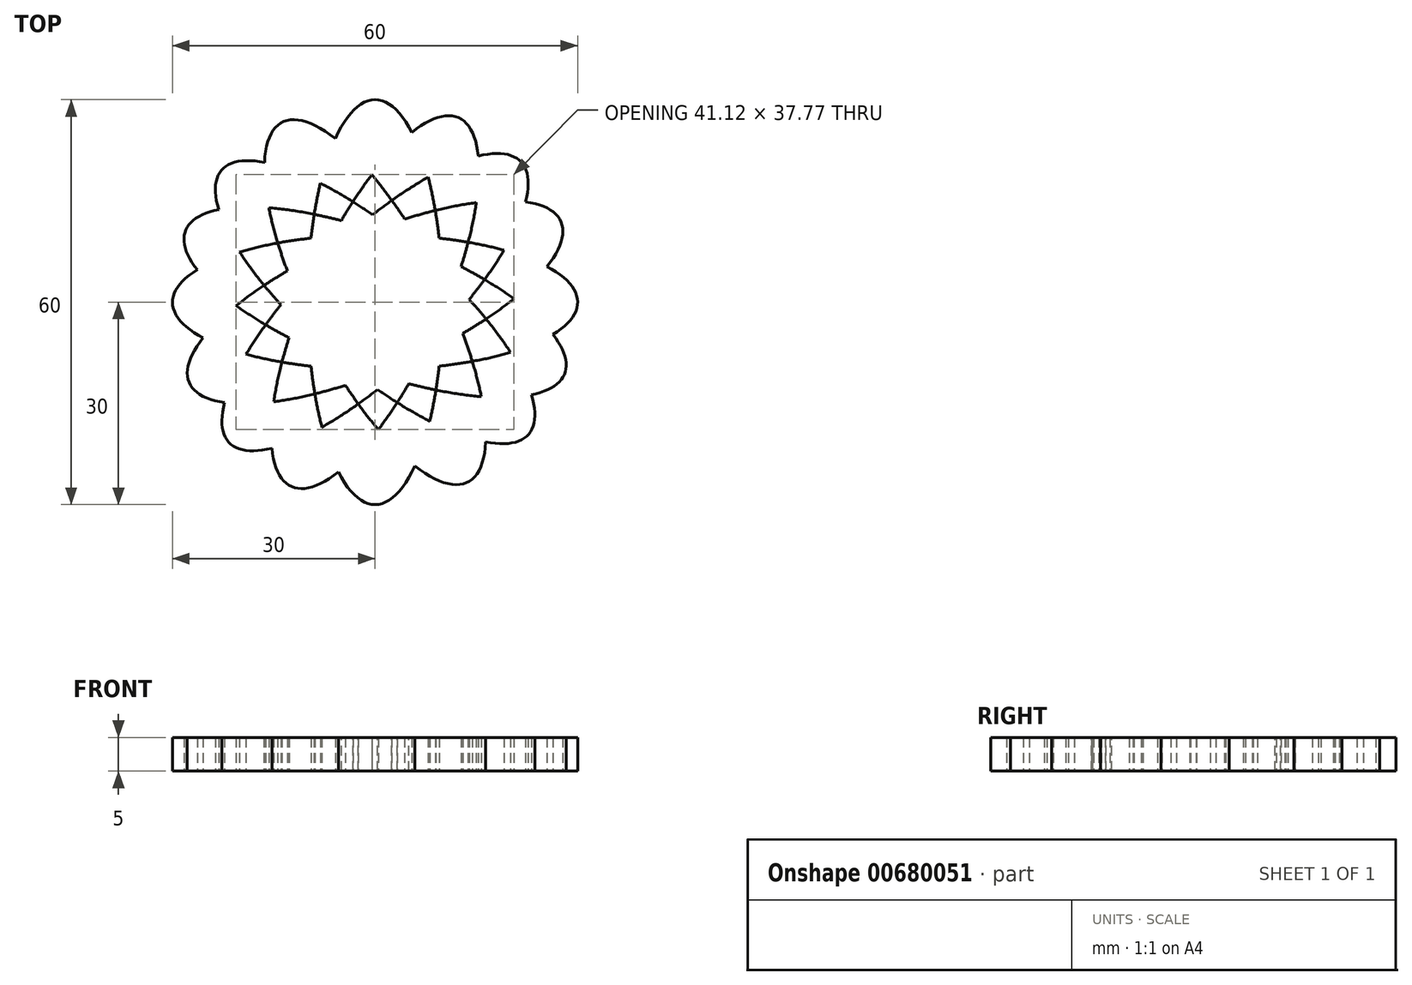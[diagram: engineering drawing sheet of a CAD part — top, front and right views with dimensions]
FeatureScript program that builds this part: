
annotation { "Feature Type Name" : "Feature", "Feature Type Description" : "" }
export const myFeature = defineFeature(function(context is Context, id is Id, definition is map)
    precondition{}
    {
        {
            var Q0;
            Q0=qCreatedBy(makeId("Top.planeOp"),FACE);
            var sketch = newSketch(context, id + "F0", { "sketchPlane" : qUnion([Q0])});
            skEllipticalArc(sketch, "E0", {});
            skEllipticalArc(sketch, "E1", {});
            skEllipticalArc(sketch, "E2", {});
            skEllipticalArc(sketch, "E3", {});
            skEllipticalArc(sketch, "E4", {});
            skEllipticalArc(sketch, "E5", {});
            skEllipticalArc(sketch, "E6", {});
            skEllipticalArc(sketch, "E7", {});
            skEllipticalArc(sketch, "E8.trimOffspring", {});
            skEllipticalArc(sketch, "E9.trimOffspring", {});
            skEllipticalArc(sketch, "E10.trimOffspring", {});
            skEllipticalArc(sketch, "E11.trimOffspring", {});
            skEllipticalArc(sketch, "E12.trimOffspring", {});
            skEllipticalArc(sketch, "E13.trimOffspring", {});
            skEllipticalArc(sketch, "E14.trimOffspring", {});
            skEllipticalArc(sketch, "E15.trimOffspring", {});
            skEllipticalArc(sketch, "E16.trimOffspring", {});
            skEllipticalArc(sketch, "E17.trimOffspring", {});
            skEllipticalArc(sketch, "E18.trimOffspring", {});
            skEllipticalArc(sketch, "E19.trimOffspring", {});
            skEllipticalArc(sketch, "E20.trimOffspring", {});
            skEllipticalArc(sketch, "E21.trimOffspring", {});
            skEllipticalArc(sketch, "E22.trimOffspring", {});
            skEllipticalArc(sketch, "E23.trimOffspring", {});
            skEllipticalArc(sketch, "E24.trimOffspring", {});
            skEllipticalArc(sketch, "E25.trimOffspring", {});
            skEllipticalArc(sketch, "E26.trimOffspring", {});
            skEllipticalArc(sketch, "E27.trimOffspring", {});
            skEllipticalArc(sketch, "E28.trimOffspring", {});
            skEllipticalArc(sketch, "E29.trimOffspring", {});
            skEllipticalArc(sketch, "E30.trimOffspring", {});
            skEllipticalArc(sketch, "E31.trimOffspring", {});
            skEllipticalArc(sketch, "E32", {});
            skEllipticalArc(sketch, "E33", {});
            skEllipticalArc(sketch, "E34", {});
            skEllipticalArc(sketch, "E35", {});
            skEllipticalArc(sketch, "E36", {});
            skEllipticalArc(sketch, "E37", {});
            skEllipticalArc(sketch, "E38", {});
            skEllipticalArc(sketch, "E39", {});
            skEllipticalArc(sketch, "E40", {});
            skEllipticalArc(sketch, "E41", {});
            skEllipticalArc(sketch, "E42", {});
            skEllipticalArc(sketch, "E43", {});
            skEllipticalArc(sketch, "E44", {});
            skEllipticalArc(sketch, "E45", {});
            skEllipticalArc(sketch, "E46", {});
            skEllipticalArc(sketch, "E47", {});
            const initialGuessF0  = {"E0": [0, 0, 0, -1, 0.03, 0.01, 5.707652658227705, 0], "E1": [0, 0, -1, 0, 0.03, 0.01, 2.642024951638131, 3.141592653589793], "E2": [0, 0, 0.719676517800556, 0.6943095201179845, 0.03, 0.01, 4.047013061400929, 5.402548984350965], "E3": [0, 0, -0.7581335094198967, 0.6520993650469777, 0.03, 0.01, 2.6137857632382424, 3.141592653589793], "E4": [0, 0, -0.45874326626276485, 0.8885688581413205, 0.03, 0.01, 2.511853225270534, 3.141592653589793], "E5": [0, 0, 0.41320832804158036, 0.9106365233379791, 0.03, 0.01, 4.109892639118385, 5.42593323517256], "E6": [0, 0, -0.9359348451973232, 0.35217320390038603, 0.03, 0.01, 2.653348630316495, 3.141592653589793], "E7": [0, 0, -0.9172268162763845, -0.3983653693576886, 0.03, 0.01, 2.584183450086654, 3.141592653589793], "E8.trimOffspring": [0, 0, 0, -1, 0.03, 0.01, 0.9425783349267141, 2.2361722457786577], "E9.trimOffspring": [0, 0, -0.45874326626276485, 0.8885688581413205, 0.03, 0.01, 3.998280747334294, 5.314885321650993], "E10.trimOffspring": [0, 0, -0.7581335094198967, 0.6520993650469777, 0.03, 0.01, 3.9802901965482214, 5.340606972252871], "E11.trimOffspring": [0, 0, -0.9359348451973232, 0.35217320390038603, 0.03, 0.01, 4.023758446463335, 5.426497213435084], "E12.trimOffspring": [0, 0, -1, 0, 0.03, 0.01, 4.022228976418415, 5.444487764221157], "E13.trimOffspring": [0, 0, 0.719676517800556, 0.6943095201179845, 0.03, 0.01, 5.78620703741481, 0], "E14.trimOffspring": [0, 0, -0.9172268162763845, -0.3983653693576886, 0.03, 0.01, 3.9988447255968187, 5.401019514306045], "E15.trimOffspring": [0, 0, 0.41320832804158036, 0.9106365233379791, 0.03, 0.01, 5.7629630431196155, 0], "E16.trimOffspring": [0, 0, 0.719676517800556, 0.6943095201179845, 0.03, 0.01, 0.9054204078111355, 2.260956330761171], "E17.trimOffspring": [0, 0, 0, -1, 0.03, 0.01, 2.566060004637914, 3.141592653589793], "E18.trimOffspring": [0, 0, 0.41320832804158036, 0.9106365233379791, 0.03, 0.01, 0.9682999855285929, 2.284340581582767], "E19.trimOffspring": [0, 0, -0.45874326626276485, 0.8885688581413205, 0.03, 0.01, 5.653445878860328, 0], "E20.trimOffspring": [0, 0, 0, -1, 0.03, 0.01, 4.084170988516508, 5.377764899368451], "E21.trimOffspring": [0, 0, -0.7581335094198967, 0.6520993650469777, 0.03, 0.01, 5.7553784168280355, 0], "E22.trimOffspring": [0, 0, -0.45874326626276485, 0.8885688581413205, 0.03, 0.01, 0.856688093744502, 2.1732926680612006], "E23.trimOffspring": [0, 0, -0.9359348451973232, 0.35217320390038603, 0.03, 0.01, 5.7949412839062875, 0], "E24.trimOffspring": [0, 0, -0.7581335094198967, 0.6520993650469777, 0.03, 0.01, 0.8386975429584291, 2.199014318663079], "E25.trimOffspring": [0, 0, -1, 0, 0.03, 0.01, 5.783617605227924, 0], "E26.trimOffspring": [0, 0, -0.9359348451973232, 0.35217320390038603, 0.03, 0.01, 0.8821657928735414, 2.284904559845293], "E27.trimOffspring": [0, 0, -0.9172268162763845, -0.3983653693576886, 0.03, 0.01, 5.725776103676448, 0], "E28.trimOffspring": [0, 0, -1, 0, 0.03, 0.01, 0.8806363228286226, 2.3028951106313644], "E29.trimOffspring": [0, 0, 0.719676517800556, 0.6943095201179845, 0.03, 0.01, 2.644614383825017, 3.141592653589793], "E30.trimOffspring": [0, 0, -0.9172268162763845, -0.3983653693576886, 0.03, 0.01, 0.857252072007026, 2.2594268607162515], "E31.trimOffspring": [0, 0, 0.41320832804158036, 0.9106365233379791, 0.03, 0.01, 2.6213703895298224, 3.141592653589793], "E32": [0, 0, -1, 0, 0.03, 0.01, 0, 0.5574092035031396], "E33": [0, 0, -0.9172268162763845, -0.3983653693576886, 0.03, 0.01, 0, 0.4969782697647762], "E34": [0, 0, 0.719676517800556, 0.6943095201179845, 0.03, 0.01, 3.141592653589793, 3.6618149176497643], "E35": [0, 0, 0.41320832804158036, 0.9106365233379791, 0.03, 0.01, 3.141592653589793, 3.7171253025416737], "E36": [0, 0, 0, -1, 0.03, 0.01, 0, 0.6297394283192591], "E37": [0, 0, -0.45874326626276485, 0.8885688581413205, 0.03, 0.01, 3.141592653589793, 3.6693995439413434], "E38": [0, 0, -0.7581335094198967, 0.6520993650469777, 0.03, 0.01, 3.141592653589793, 3.6298366768630923], "E39": [0, 0, -0.9359348451973232, 0.35217320390038603, 0.03, 0.01, 3.141592653589793, 3.6411603555414533], "E40": [0, 0, -1, 0, 0.03, 0.01, 3.141592653589793, 3.6990018570929326], "E41": [0, 0, -0.9172268162763845, -0.3983653693576886, 0.03, 0.01, 3.141592653589793, 3.6385709233545684], "E42": [0, 0, 0.719676517800556, 0.6943095201179845, 0.03, 0.01, 0, 0.5202222640599707], "E43": [0, 0, 0.41320832804158036, 0.9106365233379791, 0.03, 0.01, 0, 0.5755326489518812], "E44": [0, 0, 0, -1, 0.03, 0.01, 3.141592653589793, 3.7713320819090503], "E45": [0, 0, -0.45874326626276485, 0.8885688581413205, 0.03, 0.01, 0, 0.5278068903515505], "E46": [0, 0, -0.7581335094198967, 0.6520993650469777, 0.03, 0.01, 0, 0.48824402327329985], "E47": [0, 0, -0.9359348451973232, 0.35217320390038603, 0.03, 0.01, 0, 0.4995677019516617]};
            skSetInitialGuess(sketch, initialGuessF0);
            skSolve(sketch);
        }
        {
            var Q0;
            Q0=makeQuery(id+"F0.imprint","IMPRINT",FACE,{"disambiguationData":[TD([[makeQuery(id+"F0.imprint","IMPRINT",EDGE,{"derivedFrom":sQuery(id+"F0.wireOp",EDGE,"E0")}),1.0]])]});
            var Q1;
            {var subQ17=sQuery(id+"F0.wireOp",EDGE,"E2");var subQ21=sQuery(id+"F0.wireOp",EDGE,"E30.trimOffspring");var subQ22=makeQuery(id+"F0.imprint","INTERSECT",VERTEX,{"derivedFrom":[subQ17,subQ21]});Q1=makeQuery(id+"F0.imprint","IMPRINT",FACE,{"disambiguationData":[TD([[makeQuery(id+"F0.imprint","IMPRINT",EDGE,{"disambiguationData":[TD([[subQ22,-1.0]])],"derivedFrom":subQ17}),1.0]])]});}
            var Q2;
            {var subQ0=sQuery(id+"F0.wireOp",EDGE,"E14.trimOffspring");var subQ1=sQuery(id+"F0.wireOp",EDGE,"E9.trimOffspring");var subQ2=makeQuery(id+"F0.imprint","INTERSECT",VERTEX,{"derivedFrom":[subQ1,subQ0]});Q2=makeQuery(id+"F0.imprint","IMPRINT",FACE,{"disambiguationData":[TD([[makeQuery(id+"F0.imprint","IMPRINT",EDGE,{"disambiguationData":[TD([[subQ2,-1.0]])],"derivedFrom":subQ1}),1.0]])]});}
            var Q3;
            {var subQ0=sQuery(id+"F0.wireOp",EDGE,"E12.trimOffspring");var subQ1=sQuery(id+"F0.wireOp",EDGE,"E8.trimOffspring");var subQ2=makeQuery(id+"F0.imprint","INTERSECT",VERTEX,{"derivedFrom":[subQ1,subQ0]});Q3=makeQuery(id+"F0.imprint","IMPRINT",FACE,{"disambiguationData":[TD([[makeQuery(id+"F0.imprint","IMPRINT",EDGE,{"disambiguationData":[TD([[subQ2,-1.0]])],"derivedFrom":subQ1}),1.0]])]});}
            var Q4;
            {var subQ0=sQuery(id+"F0.wireOp",EDGE,"E11.trimOffspring");var subQ1=sQuery(id+"F0.wireOp",EDGE,"E8.trimOffspring");var subQ2=makeQuery(id+"F0.imprint","INTERSECT",VERTEX,{"derivedFrom":[subQ1,subQ0]});Q4=makeQuery(id+"F0.imprint","IMPRINT",FACE,{"disambiguationData":[TD([[makeQuery(id+"F0.imprint","IMPRINT",EDGE,{"disambiguationData":[TD([[subQ2,-1.0]])],"derivedFrom":subQ1}),1.0]])]});}
            var Q5;
            {var subQ0=sQuery(id+"F0.wireOp",EDGE,"E11.trimOffspring");var subQ1=sQuery(id+"F0.wireOp",EDGE,"E5");var subQ2=makeQuery(id+"F0.imprint","INTERSECT",VERTEX,{"derivedFrom":[subQ1,subQ0]});Q5=makeQuery(id+"F0.imprint","IMPRINT",FACE,{"disambiguationData":[TD([[makeQuery(id+"F0.imprint","IMPRINT",EDGE,{"disambiguationData":[TD([[subQ2,-1.0]])],"derivedFrom":subQ1}),1.0]])]});}
            var Q6;
            {var subQ0=sQuery(id+"F0.wireOp",EDGE,"E10.trimOffspring");var subQ1=sQuery(id+"F0.wireOp",EDGE,"E5");var subQ2=makeQuery(id+"F0.imprint","INTERSECT",VERTEX,{"derivedFrom":[subQ1,subQ0]});Q6=makeQuery(id+"F0.imprint","IMPRINT",FACE,{"disambiguationData":[TD([[makeQuery(id+"F0.imprint","IMPRINT",EDGE,{"disambiguationData":[TD([[subQ2,-1.0]])],"derivedFrom":subQ1}),1.0]])]});}
            var Q7;
            {var subQ0=sQuery(id+"F0.wireOp",EDGE,"E10.trimOffspring");var subQ1=sQuery(id+"F0.wireOp",EDGE,"E2");var subQ2=makeQuery(id+"F0.imprint","INTERSECT",VERTEX,{"derivedFrom":[subQ1,subQ0]});Q7=makeQuery(id+"F0.imprint","IMPRINT",FACE,{"disambiguationData":[TD([[makeQuery(id+"F0.imprint","IMPRINT",EDGE,{"disambiguationData":[TD([[subQ2,-1.0]])],"derivedFrom":subQ1}),1.0]])]});}
            var Q8;
            {var subQ0=sQuery(id+"F0.wireOp",EDGE,"E10.trimOffspring");var subQ1=sQuery(id+"F0.wireOp",EDGE,"E8.trimOffspring");var subQ2=makeQuery(id+"F0.imprint","INTERSECT",VERTEX,{"derivedFrom":[subQ1,subQ0]});Q8=makeQuery(id+"F0.imprint","IMPRINT",FACE,{"disambiguationData":[TD([[makeQuery(id+"F0.imprint","IMPRINT",EDGE,{"disambiguationData":[TD([[subQ2,-1.0]])],"derivedFrom":subQ1}),1.0]])]});}
            var Q9;
            {var subQ0=sQuery(id+"F0.wireOp",EDGE,"E9.trimOffspring");var subQ1=sQuery(id+"F0.wireOp",EDGE,"E2");var subQ2=makeQuery(id+"F0.imprint","INTERSECT",VERTEX,{"derivedFrom":[subQ1,subQ0]});Q9=makeQuery(id+"F0.imprint","IMPRINT",FACE,{"disambiguationData":[TD([[makeQuery(id+"F0.imprint","IMPRINT",EDGE,{"disambiguationData":[TD([[subQ2,-1.0]])],"derivedFrom":subQ1}),1.0]])]});}
            var Q10;
            {var subQ0=sQuery(id+"F0.wireOp",EDGE,"E9.trimOffspring");var subQ1=sQuery(id+"F0.wireOp",EDGE,"E2");var subQ2=makeQuery(id+"F0.imprint","INTERSECT",VERTEX,{"derivedFrom":[subQ1,subQ0]});Q10=makeQuery(id+"F0.imprint","IMPRINT",FACE,{"disambiguationData":[TD([[makeQuery(id+"F0.imprint","IMPRINT",EDGE,{"disambiguationData":[TD([[subQ2,-1.0]])],"derivedFrom":subQ1}),-1.0]])]});}
            var Q11;
            {var subQ0=sQuery(id+"F0.wireOp",EDGE,"E28.trimOffspring");var subQ1=sQuery(id+"F0.wireOp",EDGE,"E8.trimOffspring");var subQ2=makeQuery(id+"F0.imprint","INTERSECT",VERTEX,{"derivedFrom":[subQ1,subQ0]});Q11=makeQuery(id+"F0.imprint","IMPRINT",FACE,{"disambiguationData":[TD([[makeQuery(id+"F0.imprint","IMPRINT",EDGE,{"disambiguationData":[TD([[subQ2,-1.0]])],"derivedFrom":subQ1}),-1.0]])]});}
            var Q12;
            {var subQ0=sQuery(id+"F0.wireOp",EDGE,"E8.trimOffspring");var subQ1=sQuery(id+"F0.wireOp",EDGE,"E2");var subQ2=makeQuery(id+"F0.imprint","INTERSECT",VERTEX,{"derivedFrom":[subQ1,subQ0]});Q12=makeQuery(id+"F0.imprint","IMPRINT",FACE,{"disambiguationData":[TD([[makeQuery(id+"F0.imprint","IMPRINT",EDGE,{"disambiguationData":[TD([[subQ2,-1.0]])],"derivedFrom":subQ1}),1.0]])]});}
            var Q13;
            {var subQ0=sQuery(id+"F0.wireOp",EDGE,"E8.trimOffspring");var subQ1=sQuery(id+"F0.wireOp",EDGE,"E2");var subQ2=makeQuery(id+"F0.imprint","INTERSECT",VERTEX,{"derivedFrom":[subQ1,subQ0]});Q13=makeQuery(id+"F0.imprint","IMPRINT",FACE,{"disambiguationData":[TD([[makeQuery(id+"F0.imprint","IMPRINT",EDGE,{"disambiguationData":[TD([[subQ2,-1.0]])],"derivedFrom":subQ1}),-1.0]])]});}
            var Q14;
            {var subQ0=sQuery(id+"F0.wireOp",EDGE,"E5");var subQ1=sQuery(id+"F0.wireOp",EDGE,"E2");var subQ2=makeQuery(id+"F0.imprint","INTERSECT",VERTEX,{"derivedFrom":[subQ1,subQ0]});Q14=makeQuery(id+"F0.imprint","IMPRINT",FACE,{"disambiguationData":[TD([[makeQuery(id+"F0.imprint","IMPRINT",EDGE,{"disambiguationData":[TD([[subQ2,-1.0]])],"derivedFrom":subQ1}),-1.0]])]});}
            var Q15;
            {var subQ0=sQuery(id+"F0.wireOp",EDGE,"E28.trimOffspring");var subQ1=sQuery(id+"F0.wireOp",EDGE,"E5");var subQ2=makeQuery(id+"F0.imprint","INTERSECT",VERTEX,{"derivedFrom":[subQ1,subQ0]});Q15=makeQuery(id+"F0.imprint","IMPRINT",FACE,{"disambiguationData":[TD([[makeQuery(id+"F0.imprint","IMPRINT",EDGE,{"disambiguationData":[TD([[subQ2,-1.0]])],"derivedFrom":subQ1}),-1.0]])]});}
            var Q16;
            {var subQ0=sQuery(id+"F0.wireOp",EDGE,"E26.trimOffspring");var subQ1=sQuery(id+"F0.wireOp",EDGE,"E5");var subQ2=makeQuery(id+"F0.imprint","INTERSECT",VERTEX,{"derivedFrom":[subQ1,subQ0]});Q16=makeQuery(id+"F0.imprint","IMPRINT",FACE,{"disambiguationData":[TD([[makeQuery(id+"F0.imprint","IMPRINT",EDGE,{"disambiguationData":[TD([[subQ2,-1.0]])],"derivedFrom":subQ1}),-1.0]])]});}
            var Q17;
            {var subQ0=sQuery(id+"F0.wireOp",EDGE,"E24.trimOffspring");var subQ1=sQuery(id+"F0.wireOp",EDGE,"E2");var subQ2=makeQuery(id+"F0.imprint","INTERSECT",VERTEX,{"derivedFrom":[subQ1,subQ0]});Q17=makeQuery(id+"F0.imprint","IMPRINT",FACE,{"disambiguationData":[TD([[makeQuery(id+"F0.imprint","IMPRINT",EDGE,{"disambiguationData":[TD([[subQ2,-1.0]])],"derivedFrom":subQ1}),-1.0]])]});}
            var Q18;
            {var subQ0=sQuery(id+"F0.wireOp",EDGE,"E26.trimOffspring");var subQ1=sQuery(id+"F0.wireOp",EDGE,"E2");var subQ2=makeQuery(id+"F0.imprint","INTERSECT",VERTEX,{"derivedFrom":[subQ1,subQ0]});Q18=makeQuery(id+"F0.imprint","IMPRINT",FACE,{"disambiguationData":[TD([[makeQuery(id+"F0.imprint","IMPRINT",EDGE,{"disambiguationData":[TD([[subQ2,-1.0]])],"derivedFrom":subQ1}),-1.0]])]});}
            var Q19;
            {var subQ0=sQuery(id+"F0.wireOp",EDGE,"E9.trimOffspring");var subQ1=sQuery(id+"F0.wireOp",EDGE,"E5");var subQ2=makeQuery(id+"F0.imprint","INTERSECT",VERTEX,{"derivedFrom":[subQ1,subQ0]});Q19=makeQuery(id+"F0.imprint","IMPRINT",FACE,{"disambiguationData":[TD([[makeQuery(id+"F0.imprint","IMPRINT",EDGE,{"disambiguationData":[TD([[subQ2,-1.0]])],"derivedFrom":subQ1}),1.0]])]});}
            var Q20;
            {var subQ0=sQuery(id+"F0.wireOp",EDGE,"E28.trimOffspring");var subQ1=sQuery(id+"F0.wireOp",EDGE,"E2");var subQ2=makeQuery(id+"F0.imprint","INTERSECT",VERTEX,{"derivedFrom":[subQ1,subQ0]});Q20=makeQuery(id+"F0.imprint","IMPRINT",FACE,{"disambiguationData":[TD([[makeQuery(id+"F0.imprint","IMPRINT",EDGE,{"disambiguationData":[TD([[subQ2,-1.0]])],"derivedFrom":subQ1}),-1.0]])]});}
            var Q21;
            {var subQ0=sQuery(id+"F0.wireOp",EDGE,"E30.trimOffspring");var subQ1=sQuery(id+"F0.wireOp",EDGE,"E2");var subQ2=makeQuery(id+"F0.imprint","INTERSECT",VERTEX,{"derivedFrom":[subQ1,subQ0]});Q21=makeQuery(id+"F0.imprint","IMPRINT",FACE,{"disambiguationData":[TD([[makeQuery(id+"F0.imprint","IMPRINT",EDGE,{"disambiguationData":[TD([[subQ2,-1.0]])],"derivedFrom":subQ1}),-1.0]])]});}
            var Q22;
            {var subQ0=sQuery(id+"F0.wireOp",EDGE,"E5");var subQ1=sQuery(id+"F0.wireOp",EDGE,"E2");var subQ2=makeQuery(id+"F0.imprint","INTERSECT",VERTEX,{"derivedFrom":[subQ1,subQ0]});Q22=makeQuery(id+"F0.imprint","IMPRINT",FACE,{"disambiguationData":[TD([[makeQuery(id+"F0.imprint","IMPRINT",EDGE,{"disambiguationData":[TD([[subQ2,-1.0]])],"derivedFrom":subQ1}),1.0]])]});}
            var Q23;
            {var subQ0=sQuery(id+"F0.wireOp",EDGE,"E8.trimOffspring");var subQ1=sQuery(id+"F0.wireOp",EDGE,"E5");var subQ2=makeQuery(id+"F0.imprint","INTERSECT",VERTEX,{"derivedFrom":[subQ1,subQ0]});Q23=makeQuery(id+"F0.imprint","IMPRINT",FACE,{"disambiguationData":[TD([[makeQuery(id+"F0.imprint","IMPRINT",EDGE,{"disambiguationData":[TD([[subQ2,-1.0]])],"derivedFrom":subQ1}),1.0]])]});}
            var Q24;
            {var subQ0=sQuery(id+"F0.wireOp",EDGE,"E9.trimOffspring");var subQ1=sQuery(id+"F0.wireOp",EDGE,"E8.trimOffspring");var subQ2=makeQuery(id+"F0.imprint","INTERSECT",VERTEX,{"derivedFrom":[subQ1,subQ0]});Q24=makeQuery(id+"F0.imprint","IMPRINT",FACE,{"disambiguationData":[TD([[makeQuery(id+"F0.imprint","IMPRINT",EDGE,{"disambiguationData":[TD([[subQ2,-1.0]])],"derivedFrom":subQ1}),1.0]])]});}
            var Q25;
            {var subQ0=sQuery(id+"F0.wireOp",EDGE,"E10.trimOffspring");var subQ1=sQuery(id+"F0.wireOp",EDGE,"E9.trimOffspring");var subQ2=makeQuery(id+"F0.imprint","INTERSECT",VERTEX,{"derivedFrom":[subQ1,subQ0]});Q25=makeQuery(id+"F0.imprint","IMPRINT",FACE,{"disambiguationData":[TD([[makeQuery(id+"F0.imprint","IMPRINT",EDGE,{"disambiguationData":[TD([[subQ2,-1.0]])],"derivedFrom":subQ1}),1.0]])]});}
            var Q26;
            {var subQ0=sQuery(id+"F0.wireOp",EDGE,"E11.trimOffspring");var subQ1=sQuery(id+"F0.wireOp",EDGE,"E9.trimOffspring");var subQ2=makeQuery(id+"F0.imprint","INTERSECT",VERTEX,{"derivedFrom":[subQ1,subQ0]});Q26=makeQuery(id+"F0.imprint","IMPRINT",FACE,{"disambiguationData":[TD([[makeQuery(id+"F0.imprint","IMPRINT",EDGE,{"disambiguationData":[TD([[subQ2,-1.0]])],"derivedFrom":subQ1}),1.0]])]});}
            var Q27;
            {var subQ0=sQuery(id+"F0.wireOp",EDGE,"E12.trimOffspring");var subQ1=sQuery(id+"F0.wireOp",EDGE,"E9.trimOffspring");var subQ2=makeQuery(id+"F0.imprint","INTERSECT",VERTEX,{"derivedFrom":[subQ1,subQ0]});Q27=makeQuery(id+"F0.imprint","IMPRINT",FACE,{"disambiguationData":[TD([[makeQuery(id+"F0.imprint","IMPRINT",EDGE,{"disambiguationData":[TD([[subQ2,-1.0]])],"derivedFrom":subQ1}),1.0]])]});}
            var Q28;
            {var subQ0=sQuery(id+"F0.wireOp",EDGE,"E12.trimOffspring");var subQ1=sQuery(id+"F0.wireOp",EDGE,"E10.trimOffspring");var subQ2=makeQuery(id+"F0.imprint","INTERSECT",VERTEX,{"derivedFrom":[subQ1,subQ0]});Q28=makeQuery(id+"F0.imprint","IMPRINT",FACE,{"disambiguationData":[TD([[makeQuery(id+"F0.imprint","IMPRINT",EDGE,{"disambiguationData":[TD([[subQ2,-1.0]])],"derivedFrom":subQ1}),1.0]])]});}
            var Q29;
            {var subQ0=sQuery(id+"F0.wireOp",EDGE,"E11.trimOffspring");var subQ1=sQuery(id+"F0.wireOp",EDGE,"E10.trimOffspring");var subQ2=makeQuery(id+"F0.imprint","INTERSECT",VERTEX,{"derivedFrom":[subQ1,subQ0]});Q29=makeQuery(id+"F0.imprint","IMPRINT",FACE,{"disambiguationData":[TD([[makeQuery(id+"F0.imprint","IMPRINT",EDGE,{"disambiguationData":[TD([[subQ2,-1.0]])],"derivedFrom":subQ1}),1.0]])]});}
            var Q30;
            {var subQ0=sQuery(id+"F0.wireOp",EDGE,"E12.trimOffspring");var subQ1=sQuery(id+"F0.wireOp",EDGE,"E11.trimOffspring");var subQ2=makeQuery(id+"F0.imprint","INTERSECT",VERTEX,{"derivedFrom":[subQ1,subQ0]});Q30=makeQuery(id+"F0.imprint","IMPRINT",FACE,{"disambiguationData":[TD([[makeQuery(id+"F0.imprint","IMPRINT",EDGE,{"disambiguationData":[TD([[subQ2,-1.0]])],"derivedFrom":subQ1}),1.0]])]});}
            var Q31;
            {var subQ0=sQuery(id+"F0.wireOp",EDGE,"E14.trimOffspring");var subQ1=sQuery(id+"F0.wireOp",EDGE,"E11.trimOffspring");var subQ2=makeQuery(id+"F0.imprint","INTERSECT",VERTEX,{"derivedFrom":[subQ1,subQ0]});Q31=makeQuery(id+"F0.imprint","IMPRINT",FACE,{"disambiguationData":[TD([[makeQuery(id+"F0.imprint","IMPRINT",EDGE,{"disambiguationData":[TD([[subQ2,-1.0]])],"derivedFrom":subQ1}),1.0]])]});}
            var Q32;
            {var subQ0=sQuery(id+"F0.wireOp",EDGE,"E14.trimOffspring");var subQ1=sQuery(id+"F0.wireOp",EDGE,"E10.trimOffspring");var subQ2=makeQuery(id+"F0.imprint","INTERSECT",VERTEX,{"derivedFrom":[subQ1,subQ0]});Q32=makeQuery(id+"F0.imprint","IMPRINT",FACE,{"disambiguationData":[TD([[makeQuery(id+"F0.imprint","IMPRINT",EDGE,{"disambiguationData":[TD([[subQ2,-1.0]])],"derivedFrom":subQ1}),1.0]])]});}
            var Q33;
            {var subQ0=sQuery(id+"F0.wireOp",EDGE,"E14.trimOffspring");var subQ1=sQuery(id+"F0.wireOp",EDGE,"E12.trimOffspring");var subQ2=makeQuery(id+"F0.imprint","INTERSECT",VERTEX,{"derivedFrom":[subQ1,subQ0]});Q33=makeQuery(id+"F0.imprint","IMPRINT",FACE,{"disambiguationData":[TD([[makeQuery(id+"F0.imprint","IMPRINT",EDGE,{"disambiguationData":[TD([[subQ2,-1.0]])],"derivedFrom":subQ1}),1.0]])]});}
            var Q34;
            {var subQ0=sQuery(id+"F0.wireOp",EDGE,"E16.trimOffspring");var subQ1=sQuery(id+"F0.wireOp",EDGE,"E12.trimOffspring");var subQ2=makeQuery(id+"F0.imprint","INTERSECT",VERTEX,{"derivedFrom":[subQ1,subQ0]});Q34=makeQuery(id+"F0.imprint","IMPRINT",FACE,{"disambiguationData":[TD([[makeQuery(id+"F0.imprint","IMPRINT",EDGE,{"disambiguationData":[TD([[subQ2,-1.0]])],"derivedFrom":subQ1}),1.0]])]});}
            var Q35;
            {var subQ0=sQuery(id+"F0.wireOp",EDGE,"E16.trimOffspring");var subQ1=sQuery(id+"F0.wireOp",EDGE,"E11.trimOffspring");var subQ2=makeQuery(id+"F0.imprint","INTERSECT",VERTEX,{"derivedFrom":[subQ1,subQ0]});Q35=makeQuery(id+"F0.imprint","IMPRINT",FACE,{"disambiguationData":[TD([[makeQuery(id+"F0.imprint","IMPRINT",EDGE,{"disambiguationData":[TD([[subQ2,-1.0]])],"derivedFrom":subQ1}),1.0]])]});}
            var Q36;
            {var subQ0=sQuery(id+"F0.wireOp",EDGE,"E16.trimOffspring");var subQ1=sQuery(id+"F0.wireOp",EDGE,"E10.trimOffspring");var subQ2=makeQuery(id+"F0.imprint","INTERSECT",VERTEX,{"derivedFrom":[subQ1,subQ0]});Q36=makeQuery(id+"F0.imprint","IMPRINT",FACE,{"disambiguationData":[TD([[makeQuery(id+"F0.imprint","IMPRINT",EDGE,{"disambiguationData":[TD([[subQ2,-1.0]])],"derivedFrom":subQ1}),1.0]])]});}
            var Q37;
            {var subQ0=sQuery(id+"F0.wireOp",EDGE,"E16.trimOffspring");var subQ1=sQuery(id+"F0.wireOp",EDGE,"E14.trimOffspring");var subQ2=makeQuery(id+"F0.imprint","INTERSECT",VERTEX,{"derivedFrom":[subQ1,subQ0]});Q37=makeQuery(id+"F0.imprint","IMPRINT",FACE,{"disambiguationData":[TD([[makeQuery(id+"F0.imprint","IMPRINT",EDGE,{"disambiguationData":[TD([[subQ2,-1.0]])],"derivedFrom":subQ1}),1.0]])]});}
            var Q38;
            {var subQ0=sQuery(id+"F0.wireOp",EDGE,"E18.trimOffspring");var subQ1=sQuery(id+"F0.wireOp",EDGE,"E14.trimOffspring");var subQ2=makeQuery(id+"F0.imprint","INTERSECT",VERTEX,{"derivedFrom":[subQ1,subQ0]});Q38=makeQuery(id+"F0.imprint","IMPRINT",FACE,{"disambiguationData":[TD([[makeQuery(id+"F0.imprint","IMPRINT",EDGE,{"disambiguationData":[TD([[subQ2,-1.0]])],"derivedFrom":subQ1}),1.0]])]});}
            var Q39;
            {var subQ0=sQuery(id+"F0.wireOp",EDGE,"E18.trimOffspring");var subQ1=sQuery(id+"F0.wireOp",EDGE,"E16.trimOffspring");var subQ2=makeQuery(id+"F0.imprint","INTERSECT",VERTEX,{"derivedFrom":[subQ1,subQ0]});Q39=makeQuery(id+"F0.imprint","IMPRINT",FACE,{"disambiguationData":[TD([[makeQuery(id+"F0.imprint","IMPRINT",EDGE,{"disambiguationData":[TD([[subQ2,-1.0]])],"derivedFrom":subQ1}),1.0]])]});}
            var Q40;
            {var subQ0=sQuery(id+"F0.wireOp",EDGE,"E18.trimOffspring");var subQ1=sQuery(id+"F0.wireOp",EDGE,"E12.trimOffspring");var subQ2=makeQuery(id+"F0.imprint","INTERSECT",VERTEX,{"derivedFrom":[subQ1,subQ0]});Q40=makeQuery(id+"F0.imprint","IMPRINT",FACE,{"disambiguationData":[TD([[makeQuery(id+"F0.imprint","IMPRINT",EDGE,{"disambiguationData":[TD([[subQ2,-1.0]])],"derivedFrom":subQ1}),1.0]])]});}
            var Q41;
            {var subQ0=sQuery(id+"F0.wireOp",EDGE,"E18.trimOffspring");var subQ1=sQuery(id+"F0.wireOp",EDGE,"E11.trimOffspring");var subQ2=makeQuery(id+"F0.imprint","INTERSECT",VERTEX,{"derivedFrom":[subQ1,subQ0]});Q41=makeQuery(id+"F0.imprint","IMPRINT",FACE,{"disambiguationData":[TD([[makeQuery(id+"F0.imprint","IMPRINT",EDGE,{"disambiguationData":[TD([[subQ2,-1.0]])],"derivedFrom":subQ1}),1.0]])]});}
            var Q42;
            {var subQ0=sQuery(id+"F0.wireOp",EDGE,"E20.trimOffspring");var subQ1=sQuery(id+"F0.wireOp",EDGE,"E12.trimOffspring");var subQ2=makeQuery(id+"F0.imprint","INTERSECT",VERTEX,{"derivedFrom":[subQ1,subQ0]});Q42=makeQuery(id+"F0.imprint","IMPRINT",FACE,{"disambiguationData":[TD([[makeQuery(id+"F0.imprint","IMPRINT",EDGE,{"disambiguationData":[TD([[subQ2,-1.0]])],"derivedFrom":subQ1}),1.0]])]});}
            var Q43;
            {var subQ0=sQuery(id+"F0.wireOp",EDGE,"E22.trimOffspring");var subQ1=sQuery(id+"F0.wireOp",EDGE,"E14.trimOffspring");var subQ2=makeQuery(id+"F0.imprint","INTERSECT",VERTEX,{"derivedFrom":[subQ1,subQ0]});Q43=makeQuery(id+"F0.imprint","IMPRINT",FACE,{"disambiguationData":[TD([[makeQuery(id+"F0.imprint","IMPRINT",EDGE,{"disambiguationData":[TD([[subQ2,-1.0]])],"derivedFrom":subQ1}),1.0]])]});}
            var Q44;
            {var subQ0=sQuery(id+"F0.wireOp",EDGE,"E20.trimOffspring");var subQ1=sQuery(id+"F0.wireOp",EDGE,"E14.trimOffspring");var subQ2=makeQuery(id+"F0.imprint","INTERSECT",VERTEX,{"derivedFrom":[subQ1,subQ0]});Q44=makeQuery(id+"F0.imprint","IMPRINT",FACE,{"disambiguationData":[TD([[makeQuery(id+"F0.imprint","IMPRINT",EDGE,{"disambiguationData":[TD([[subQ2,-1.0]])],"derivedFrom":subQ1}),1.0]])]});}
            var Q45;
            {var subQ0=sQuery(id+"F0.wireOp",EDGE,"E20.trimOffspring");var subQ1=sQuery(id+"F0.wireOp",EDGE,"E16.trimOffspring");var subQ2=makeQuery(id+"F0.imprint","INTERSECT",VERTEX,{"derivedFrom":[subQ1,subQ0]});Q45=makeQuery(id+"F0.imprint","IMPRINT",FACE,{"disambiguationData":[TD([[makeQuery(id+"F0.imprint","IMPRINT",EDGE,{"disambiguationData":[TD([[subQ2,-1.0]])],"derivedFrom":subQ1}),1.0]])]});}
            var Q46;
            {var subQ0=sQuery(id+"F0.wireOp",EDGE,"E20.trimOffspring");var subQ1=sQuery(id+"F0.wireOp",EDGE,"E18.trimOffspring");var subQ2=makeQuery(id+"F0.imprint","INTERSECT",VERTEX,{"derivedFrom":[subQ1,subQ0]});Q46=makeQuery(id+"F0.imprint","IMPRINT",FACE,{"disambiguationData":[TD([[makeQuery(id+"F0.imprint","IMPRINT",EDGE,{"disambiguationData":[TD([[subQ2,-1.0]])],"derivedFrom":subQ1}),1.0]])]});}
            var Q47;
            {var subQ0=sQuery(id+"F0.wireOp",EDGE,"E22.trimOffspring");var subQ1=sQuery(id+"F0.wireOp",EDGE,"E16.trimOffspring");var subQ2=makeQuery(id+"F0.imprint","INTERSECT",VERTEX,{"derivedFrom":[subQ1,subQ0]});Q47=makeQuery(id+"F0.imprint","IMPRINT",FACE,{"disambiguationData":[TD([[makeQuery(id+"F0.imprint","IMPRINT",EDGE,{"disambiguationData":[TD([[subQ2,-1.0]])],"derivedFrom":subQ1}),1.0]])]});}
            var Q48;
            {var subQ0=sQuery(id+"F0.wireOp",EDGE,"E22.trimOffspring");var subQ1=sQuery(id+"F0.wireOp",EDGE,"E18.trimOffspring");var subQ2=makeQuery(id+"F0.imprint","INTERSECT",VERTEX,{"derivedFrom":[subQ1,subQ0]});Q48=makeQuery(id+"F0.imprint","IMPRINT",FACE,{"disambiguationData":[TD([[makeQuery(id+"F0.imprint","IMPRINT",EDGE,{"disambiguationData":[TD([[subQ2,-1.0]])],"derivedFrom":subQ1}),1.0]])]});}
            var Q49;
            {var subQ0=sQuery(id+"F0.wireOp",EDGE,"E24.trimOffspring");var subQ1=sQuery(id+"F0.wireOp",EDGE,"E16.trimOffspring");var subQ2=makeQuery(id+"F0.imprint","INTERSECT",VERTEX,{"derivedFrom":[subQ1,subQ0]});Q49=makeQuery(id+"F0.imprint","IMPRINT",FACE,{"disambiguationData":[TD([[makeQuery(id+"F0.imprint","IMPRINT",EDGE,{"disambiguationData":[TD([[subQ2,-1.0]])],"derivedFrom":subQ1}),1.0]])]});}
            var Q50;
            {var subQ0=sQuery(id+"F0.wireOp",EDGE,"E24.trimOffspring");var subQ1=sQuery(id+"F0.wireOp",EDGE,"E18.trimOffspring");var subQ2=makeQuery(id+"F0.imprint","INTERSECT",VERTEX,{"derivedFrom":[subQ1,subQ0]});Q50=makeQuery(id+"F0.imprint","IMPRINT",FACE,{"disambiguationData":[TD([[makeQuery(id+"F0.imprint","IMPRINT",EDGE,{"disambiguationData":[TD([[subQ2,-1.0]])],"derivedFrom":subQ1}),1.0]])]});}
            var Q51;
            {var subQ0=sQuery(id+"F0.wireOp",EDGE,"E26.trimOffspring");var subQ1=sQuery(id+"F0.wireOp",EDGE,"E18.trimOffspring");var subQ2=makeQuery(id+"F0.imprint","INTERSECT",VERTEX,{"derivedFrom":[subQ1,subQ0]});Q51=makeQuery(id+"F0.imprint","IMPRINT",FACE,{"disambiguationData":[TD([[makeQuery(id+"F0.imprint","IMPRINT",EDGE,{"disambiguationData":[TD([[subQ2,-1.0]])],"derivedFrom":subQ1}),1.0]])]});}
            var Q52;
            {var subQ0=sQuery(id+"F0.wireOp",EDGE,"E24.trimOffspring");var subQ1=sQuery(id+"F0.wireOp",EDGE,"E20.trimOffspring");var subQ2=makeQuery(id+"F0.imprint","INTERSECT",VERTEX,{"derivedFrom":[subQ1,subQ0]});Q52=makeQuery(id+"F0.imprint","IMPRINT",FACE,{"disambiguationData":[TD([[makeQuery(id+"F0.imprint","IMPRINT",EDGE,{"disambiguationData":[TD([[subQ2,-1.0]])],"derivedFrom":subQ1}),1.0]])]});}
            var Q53;
            {var subQ0=sQuery(id+"F0.wireOp",EDGE,"E22.trimOffspring");var subQ1=sQuery(id+"F0.wireOp",EDGE,"E20.trimOffspring");var subQ2=makeQuery(id+"F0.imprint","INTERSECT",VERTEX,{"derivedFrom":[subQ1,subQ0]});Q53=makeQuery(id+"F0.imprint","IMPRINT",FACE,{"disambiguationData":[TD([[makeQuery(id+"F0.imprint","IMPRINT",EDGE,{"disambiguationData":[TD([[subQ2,-1.0]])],"derivedFrom":subQ1}),1.0]])]});}
            var Q54;
            {var subQ0=sQuery(id+"F0.wireOp",EDGE,"E26.trimOffspring");var subQ1=sQuery(id+"F0.wireOp",EDGE,"E20.trimOffspring");var subQ2=makeQuery(id+"F0.imprint","INTERSECT",VERTEX,{"derivedFrom":[subQ1,subQ0]});Q54=makeQuery(id+"F0.imprint","IMPRINT",FACE,{"disambiguationData":[TD([[makeQuery(id+"F0.imprint","IMPRINT",EDGE,{"disambiguationData":[TD([[subQ2,-1.0]])],"derivedFrom":subQ1}),1.0]])]});}
            var Q55;
            {var subQ0=sQuery(id+"F0.wireOp",EDGE,"E24.trimOffspring");var subQ1=sQuery(id+"F0.wireOp",EDGE,"E22.trimOffspring");var subQ2=makeQuery(id+"F0.imprint","INTERSECT",VERTEX,{"derivedFrom":[subQ1,subQ0]});Q55=makeQuery(id+"F0.imprint","IMPRINT",FACE,{"disambiguationData":[TD([[makeQuery(id+"F0.imprint","IMPRINT",EDGE,{"disambiguationData":[TD([[subQ2,-1.0]])],"derivedFrom":subQ1}),1.0]])]});}
            var Q56;
            {var subQ0=sQuery(id+"F0.wireOp",EDGE,"E26.trimOffspring");var subQ1=sQuery(id+"F0.wireOp",EDGE,"E22.trimOffspring");var subQ2=makeQuery(id+"F0.imprint","INTERSECT",VERTEX,{"derivedFrom":[subQ1,subQ0]});Q56=makeQuery(id+"F0.imprint","IMPRINT",FACE,{"disambiguationData":[TD([[makeQuery(id+"F0.imprint","IMPRINT",EDGE,{"disambiguationData":[TD([[subQ2,-1.0]])],"derivedFrom":subQ1}),1.0]])]});}
            var Q57;
            {var subQ0=sQuery(id+"F0.wireOp",EDGE,"E28.trimOffspring");var subQ1=sQuery(id+"F0.wireOp",EDGE,"E20.trimOffspring");var subQ2=makeQuery(id+"F0.imprint","INTERSECT",VERTEX,{"derivedFrom":[subQ1,subQ0]});Q57=makeQuery(id+"F0.imprint","IMPRINT",FACE,{"disambiguationData":[TD([[makeQuery(id+"F0.imprint","IMPRINT",EDGE,{"disambiguationData":[TD([[subQ2,-1.0]])],"derivedFrom":subQ1}),1.0]])]});}
            var Q58;
            {var subQ0=sQuery(id+"F0.wireOp",EDGE,"E28.trimOffspring");var subQ1=sQuery(id+"F0.wireOp",EDGE,"E22.trimOffspring");var subQ2=makeQuery(id+"F0.imprint","INTERSECT",VERTEX,{"derivedFrom":[subQ1,subQ0]});Q58=makeQuery(id+"F0.imprint","IMPRINT",FACE,{"disambiguationData":[TD([[makeQuery(id+"F0.imprint","IMPRINT",EDGE,{"disambiguationData":[TD([[subQ2,-1.0]])],"derivedFrom":subQ1}),1.0]])]});}
            var Q59;
            {var subQ0=sQuery(id+"F0.wireOp",EDGE,"E28.trimOffspring");var subQ1=sQuery(id+"F0.wireOp",EDGE,"E24.trimOffspring");var subQ2=makeQuery(id+"F0.imprint","INTERSECT",VERTEX,{"derivedFrom":[subQ1,subQ0]});Q59=makeQuery(id+"F0.imprint","IMPRINT",FACE,{"disambiguationData":[TD([[makeQuery(id+"F0.imprint","IMPRINT",EDGE,{"disambiguationData":[TD([[subQ2,-1.0]])],"derivedFrom":subQ1}),1.0]])]});}
            var Q60;
            {var subQ0=sQuery(id+"F0.wireOp",EDGE,"E26.trimOffspring");var subQ1=sQuery(id+"F0.wireOp",EDGE,"E24.trimOffspring");var subQ2=makeQuery(id+"F0.imprint","INTERSECT",VERTEX,{"derivedFrom":[subQ1,subQ0]});Q60=makeQuery(id+"F0.imprint","IMPRINT",FACE,{"disambiguationData":[TD([[makeQuery(id+"F0.imprint","IMPRINT",EDGE,{"disambiguationData":[TD([[subQ2,-1.0]])],"derivedFrom":subQ1}),1.0]])]});}
            var Q61;
            {var subQ0=sQuery(id+"F0.wireOp",EDGE,"E28.trimOffspring");var subQ1=sQuery(id+"F0.wireOp",EDGE,"E26.trimOffspring");var subQ2=makeQuery(id+"F0.imprint","INTERSECT",VERTEX,{"derivedFrom":[subQ1,subQ0]});Q61=makeQuery(id+"F0.imprint","IMPRINT",FACE,{"disambiguationData":[TD([[makeQuery(id+"F0.imprint","IMPRINT",EDGE,{"disambiguationData":[TD([[subQ2,-1.0]])],"derivedFrom":subQ1}),1.0]])]});}
            var Q62;
            {var subQ0=sQuery(id+"F0.wireOp",EDGE,"E28.trimOffspring");var subQ1=sQuery(id+"F0.wireOp",EDGE,"E2");var subQ2=makeQuery(id+"F0.imprint","INTERSECT",VERTEX,{"derivedFrom":[subQ1,subQ0]});Q62=makeQuery(id+"F0.imprint","IMPRINT",FACE,{"disambiguationData":[TD([[makeQuery(id+"F0.imprint","IMPRINT",EDGE,{"disambiguationData":[TD([[subQ2,-1.0]])],"derivedFrom":subQ1}),1.0]])]});}
            var Q63;
            {var subQ0=sQuery(id+"F0.wireOp",EDGE,"E26.trimOffspring");var subQ1=sQuery(id+"F0.wireOp",EDGE,"E2");var subQ2=makeQuery(id+"F0.imprint","INTERSECT",VERTEX,{"derivedFrom":[subQ1,subQ0]});Q63=makeQuery(id+"F0.imprint","IMPRINT",FACE,{"disambiguationData":[TD([[makeQuery(id+"F0.imprint","IMPRINT",EDGE,{"disambiguationData":[TD([[subQ2,-1.0]])],"derivedFrom":subQ1}),1.0]])]});}
            var Q64;
            {var subQ0=sQuery(id+"F0.wireOp",EDGE,"E24.trimOffspring");var subQ1=sQuery(id+"F0.wireOp",EDGE,"E2");var subQ2=makeQuery(id+"F0.imprint","INTERSECT",VERTEX,{"derivedFrom":[subQ1,subQ0]});Q64=makeQuery(id+"F0.imprint","IMPRINT",FACE,{"disambiguationData":[TD([[makeQuery(id+"F0.imprint","IMPRINT",EDGE,{"disambiguationData":[TD([[subQ2,-1.0]])],"derivedFrom":subQ1}),1.0]])]});}
            var Q65;
            {var subQ0=sQuery(id+"F0.wireOp",EDGE,"E22.trimOffspring");var subQ1=sQuery(id+"F0.wireOp",EDGE,"E2");var subQ2=makeQuery(id+"F0.imprint","INTERSECT",VERTEX,{"derivedFrom":[subQ1,subQ0]});Q65=makeQuery(id+"F0.imprint","IMPRINT",FACE,{"disambiguationData":[TD([[makeQuery(id+"F0.imprint","IMPRINT",EDGE,{"disambiguationData":[TD([[subQ2,-1.0]])],"derivedFrom":subQ1}),1.0]])]});}
            extrude(context, id + "F1", {"entities" : qUnion([Q0, Q1, Q2, Q3, Q4, Q5, Q6, Q7, Q8, Q9, Q10, Q11, Q12, Q13, Q14, Q15, Q16, Q17, Q18, Q19, Q20, Q21, Q22, Q23, Q24, Q25, Q26, Q27, Q28, Q29, Q30, Q31, Q32, Q33, Q34, Q35, Q36, Q37, Q38, Q39, Q40, Q41, Q42, Q43, Q44, Q45, Q46, Q47, Q48, Q49, Q50, Q51, Q52, Q53, Q54, Q55, Q56, Q57, Q58, Q59, Q60, Q61, Q62, Q63, Q64, Q65]), "depth" : 5 * mm, "offsetDistance" : 25 * mm});
        }
    });
